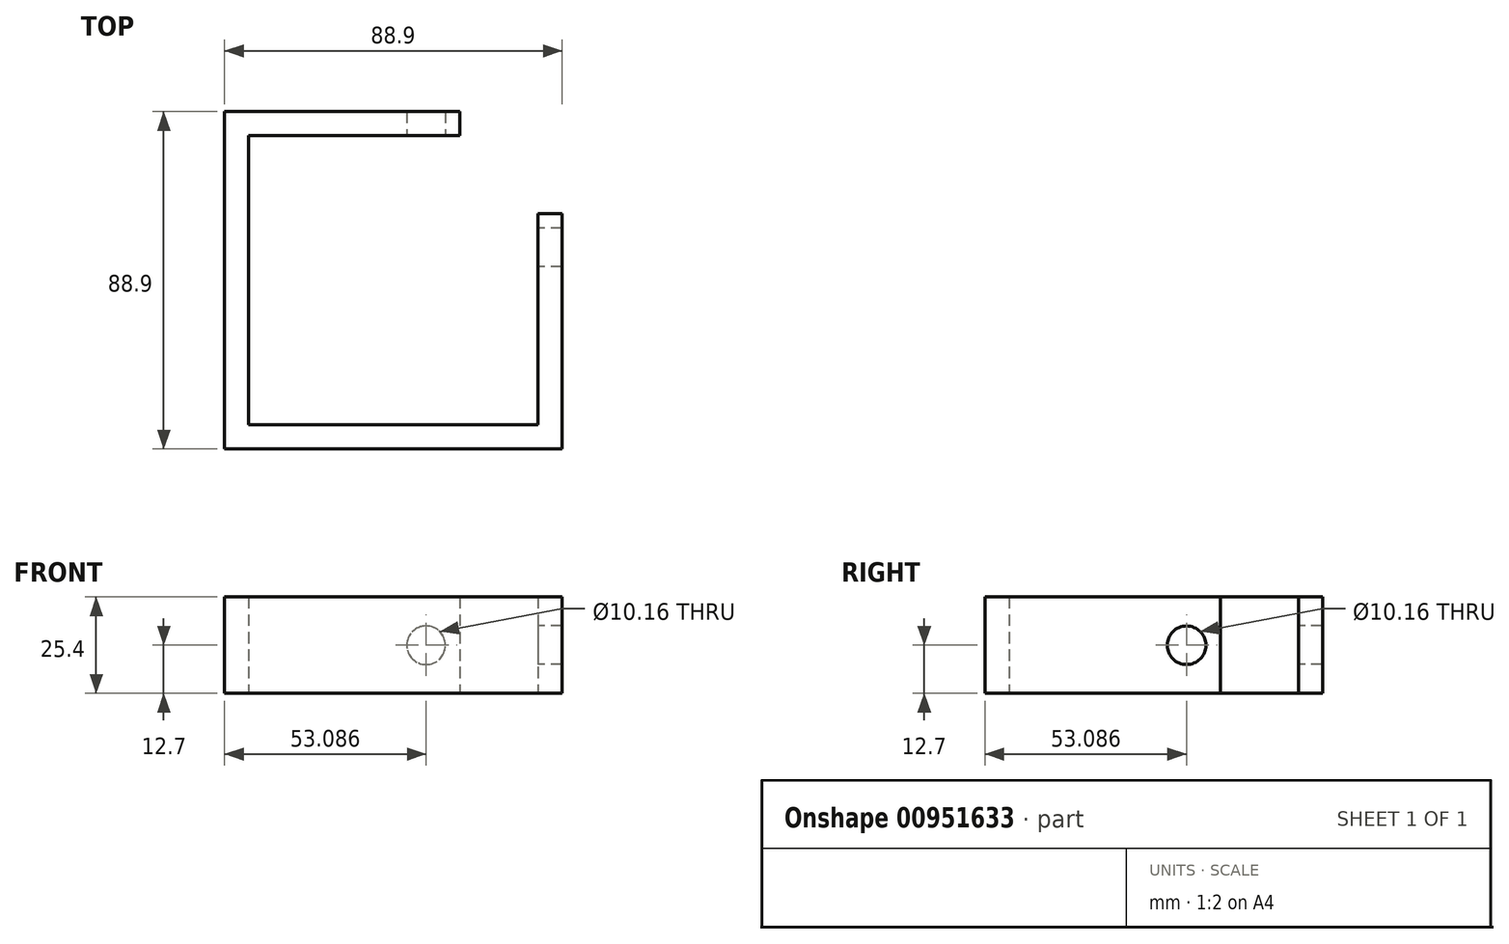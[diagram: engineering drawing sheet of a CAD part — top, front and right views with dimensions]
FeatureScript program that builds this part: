
annotation { "Feature Type Name" : "Feature", "Feature Type Description" : "" }
export const myFeature = defineFeature(function(context is Context, id is Id, definition is map)
    precondition{}
    {
        {
            var Q0;
            Q0=qCreatedBy(makeId("Top.planeOp"),FACE);
            var sketch = newSketch(context, id + "F0", { "sketchPlane" : qUnion([Q0])});
            skLineSegment(sketch, "E0", {"start": v(-82.55, 6.35) * mm, "end": v(-20.57, 6.35) * mm});
            skLineSegment(sketch, "E1", {"start": v(6.35, -20.57) * mm, "end": v(6.35, -82.55) * mm});
            skLineSegment(sketch, "E2", {"start": v(0, -76.2) * mm, "end": v(0, -20.57) * mm});
            skLineSegment(sketch, "E3", {"start": v(-20.57, 0) * mm, "end": v(-76.2, 0) * mm});
            skLineSegment(sketch, "E4", {"start": v(-29.46, 0) * mm, "end": v(-29.46, 6.35) * mm, "construction": true});
            skLineSegment(sketch, "E5", {"start": v(-20.57, 6.35) * mm, "end": v(-20.57, 0) * mm});
            skLineSegment(sketch, "E6", {"start": v(0, -20.57) * mm, "end": v(6.35, -20.57) * mm});
            skLineSegment(sketch, "E7", {"start": v(-82.55, 6.35) * mm, "end": v(-82.55, -82.55) * mm});
            skLineSegment(sketch, "E8", {"start": v(-82.55, -82.55) * mm, "end": v(6.35, -82.55) * mm});
            skLineSegment(sketch, "E9", {"start": v(-76.2, 0) * mm, "end": v(-76.2, -76.2) * mm});
            skLineSegment(sketch, "E10", {"start": v(-76.2, -76.2) * mm, "end": v(0, -76.2) * mm});
            skPoint(sketch, "E11.orphan", {"position": v(0, 0) * mm});
            skLineSegment(sketch, "E12", {"start": v(-20.57, 0) * mm, "end": v(0, -20.57) * mm, "construction": true});
            skLineSegment(sketch, "E13", {"start": v(0, 0) * mm, "end": v(-10.29, -10.29) * mm, "construction": true});
            skLineSegment(sketch, "E14", {"start": v(0, -29.46) * mm, "end": v(6.35, -29.46) * mm, "construction": true});
            skSolve(sketch);
        }
        {
            var Q0;
            Q0 = qSketchRegion(id + "F0", true);
            extrude(context, id + "F1", {"entities" : qUnion([Q0]), "depth" : 25.4 * mm, "offsetDistance" : 25.4 * mm});
        }
        {
            var Q0;
            Q0=makeQuery(id+"F1.opExtrude","SWEPT_FACE",FACE,{"disambiguationData":[OSD([sQuery(id+"F0.wireOp",EDGE,"E3")])]});
            var sketch = newSketch(context, id + "F2", { "sketchPlane" : qUnion([Q0])});
            skCircle(sketch, "E15", {"center": v(-29.46, 12.7) * mm, "radius": 5.08 * mm});
            skLineSegment(sketch, "E16", {"start": v(-29.46, 12.7) * mm, "end": v(-20.57, 12.7) * mm});
            skSolve(sketch);
        }
        {
            var Q0;
            Q0 = qSketchRegion(id + "F2", true);
            extrude(context, id + "F3", {"entities" : qUnion([Q0]), "operationType" : NewBodyOperationType.REMOVE, "oppositeDirection" : true, "depth" : 12.7 * mm, "offsetDistance" : 25.4 * mm});
        }
        {
            var Q0;
            Q0=makeQuery(id+"F1.opExtrude","SWEPT_FACE",FACE,{"disambiguationData":[OSD([sQuery(id+"F0.wireOp",EDGE,"E2")])]});
            var sketch = newSketch(context, id + "F4", { "sketchPlane" : qUnion([Q0])});
            skCircle(sketch, "E17", {"center": v(29.46, 12.7) * mm, "radius": 5.08 * mm});
            skLineSegment(sketch, "E18", {"start": v(48.39, 25.4) * mm, "end": v(48.39, 25.4) * mm});
            skLineSegment(sketch, "E19", {"start": v(29.46, 12.7) * mm, "end": v(20.57, 12.7) * mm, "construction": true});
            skSolve(sketch);
        }
        {
            var Q0;
            Q0 = qSketchRegion(id + "F4", true);
            extrude(context, id + "F5", {"entities" : qUnion([Q0]), "operationType" : NewBodyOperationType.REMOVE, "endBound" : BoundingType.THROUGH_ALL, "oppositeDirection" : true, "depth" : 12.7 * mm, "offsetDistance" : 25.4 * mm});
        }
    });
